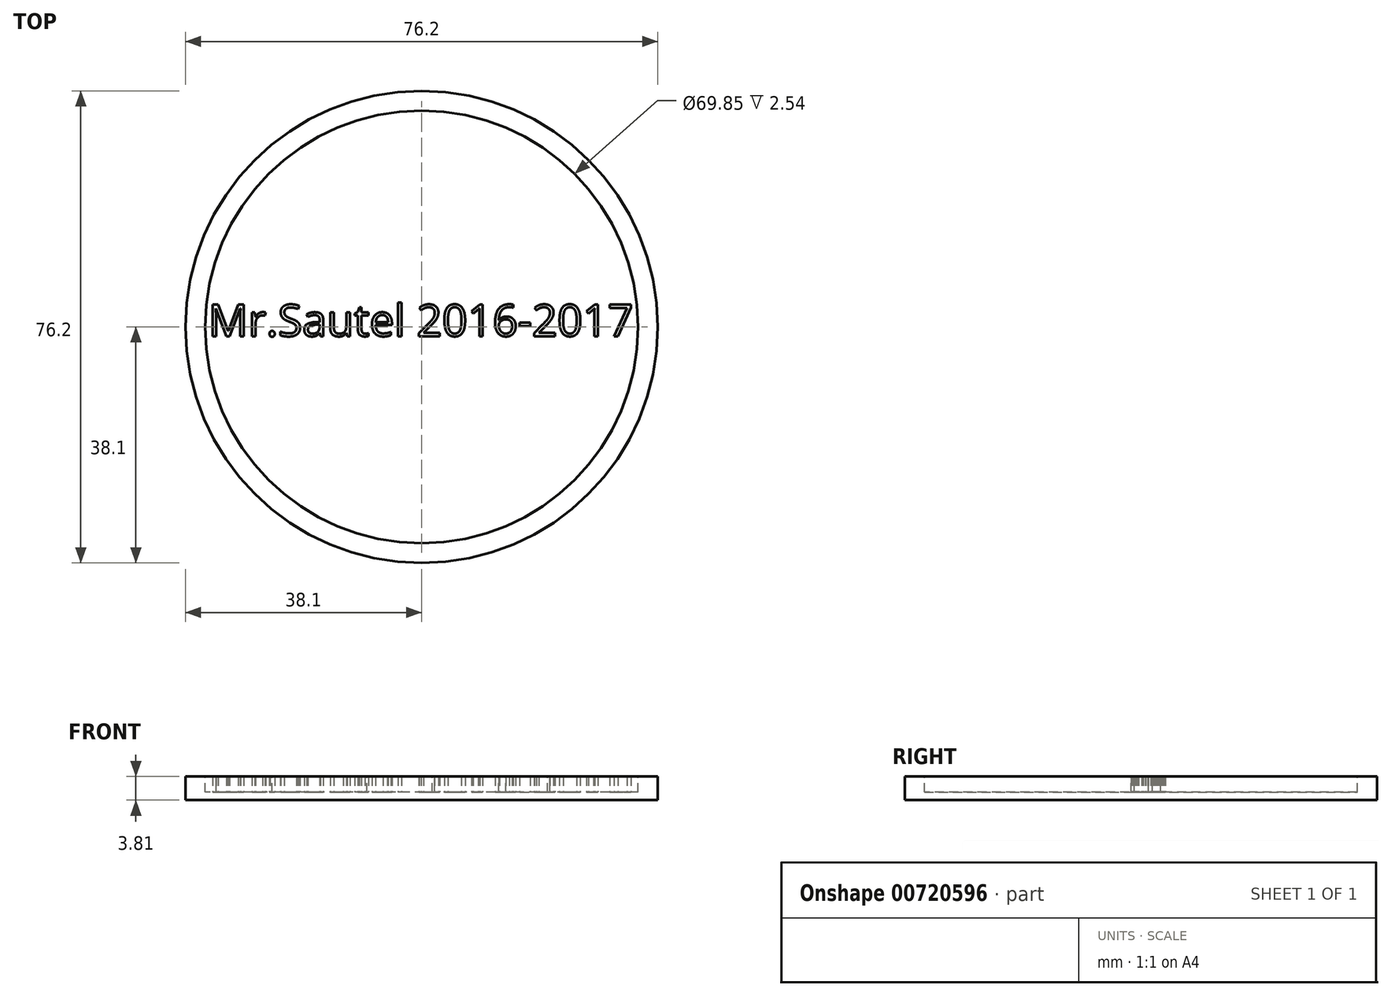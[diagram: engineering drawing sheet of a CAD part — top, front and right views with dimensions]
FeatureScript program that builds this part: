
annotation { "Feature Type Name" : "Feature", "Feature Type Description" : "" }
export const myFeature = defineFeature(function(context is Context, id is Id, definition is map)
    precondition{}
    {
        {
            var Q0;
            Q0=qCreatedBy(makeId("Top.planeOp"),FACE);
            var sketch = newSketch(context, id + "F0", { "sketchPlane" : qUnion([Q0])});
            skCircle(sketch, "E0", {"center": v(0, 0) * mm, "radius": 38.1 * mm});
            skSolve(sketch);
        }
        {
            var Q0;
            Q0=makeQuery(id+"F0.imprint","IMPRINT",FACE,{"disambiguationData":[TD([[makeQuery(id+"F0.imprint","IMPRINT",EDGE,{"derivedFrom":sQuery(id+"F0.wireOp",EDGE,"E0")}),1.0]])]});
            extrude(context, id + "F1", {"entities" : qUnion([Q0]), "depth" : 3.8 * mm, "offsetDistance" : 25.4 * mm});
        }
        {
            var Q0;
            Q0=makeQuery(id+"F1.opExtrude","CAP_FACE",FACE,{"disambiguationData":[OSD([sQuery(id+"F0.wireOp",EDGE,"E0")])],"isStart":false});
            var sketch = newSketch(context, id + "F2", { "sketchPlane" : qUnion([Q0])});
            skCircle(sketch, "E1", {"center": v(0, 0) * mm, "radius": 34.93 * mm});
            skSolve(sketch);
        }
        {
            var Q0;
            Q0=makeQuery(id+"F2.imprint","IMPRINT",FACE,{"disambiguationData":[TD([[makeQuery(id+"F2.imprint","IMPRINT",EDGE,{"derivedFrom":sQuery(id+"F2.wireOp",EDGE,"E1")}),1.0]])]});
            extrude(context, id + "F3", {"entities" : qUnion([Q0]), "operationType" : NewBodyOperationType.REMOVE, "oppositeDirection" : true, "depth" : 2.54 * mm, "offsetDistance" : 25.4 * mm});
        }
        {
            var Q0;
            Q0=makeQuery(id+"F3.boolean.opBoolean","COPY",FACE,{"derivedFrom":makeQuery(id+"F3.opExtrude","CAP_FACE",FACE,{"disambiguationData":[OSD([sQuery(id+"F2.wireOp",EDGE,"E1")])],"isStart":false})});
            var sketch = newSketch(context, id + "F4", { "sketchPlane" : qUnion([Q0])});
            skText(sketch, "E2", { "text": "Mr.Sautel 2016-2017", "fontName": "OpenSans-Regular.ttf"});
            const initialGuessF4  = {"E2": [-0.03442, -0.00149, 1, 0, 0.00513]};
            skSetInitialGuess(sketch, initialGuessF4);
            skSolve(sketch);
        }
        {
            var Q0;
            Q0=qSketchRegion(id+"F4",true);
            extrude(context, id + "F5", {"entities" : qUnion([Q0]), "operationType" : NewBodyOperationType.ADD, "depth" : 2.54 * mm, "offsetDistance" : 25.4 * mm});
        }
    });
